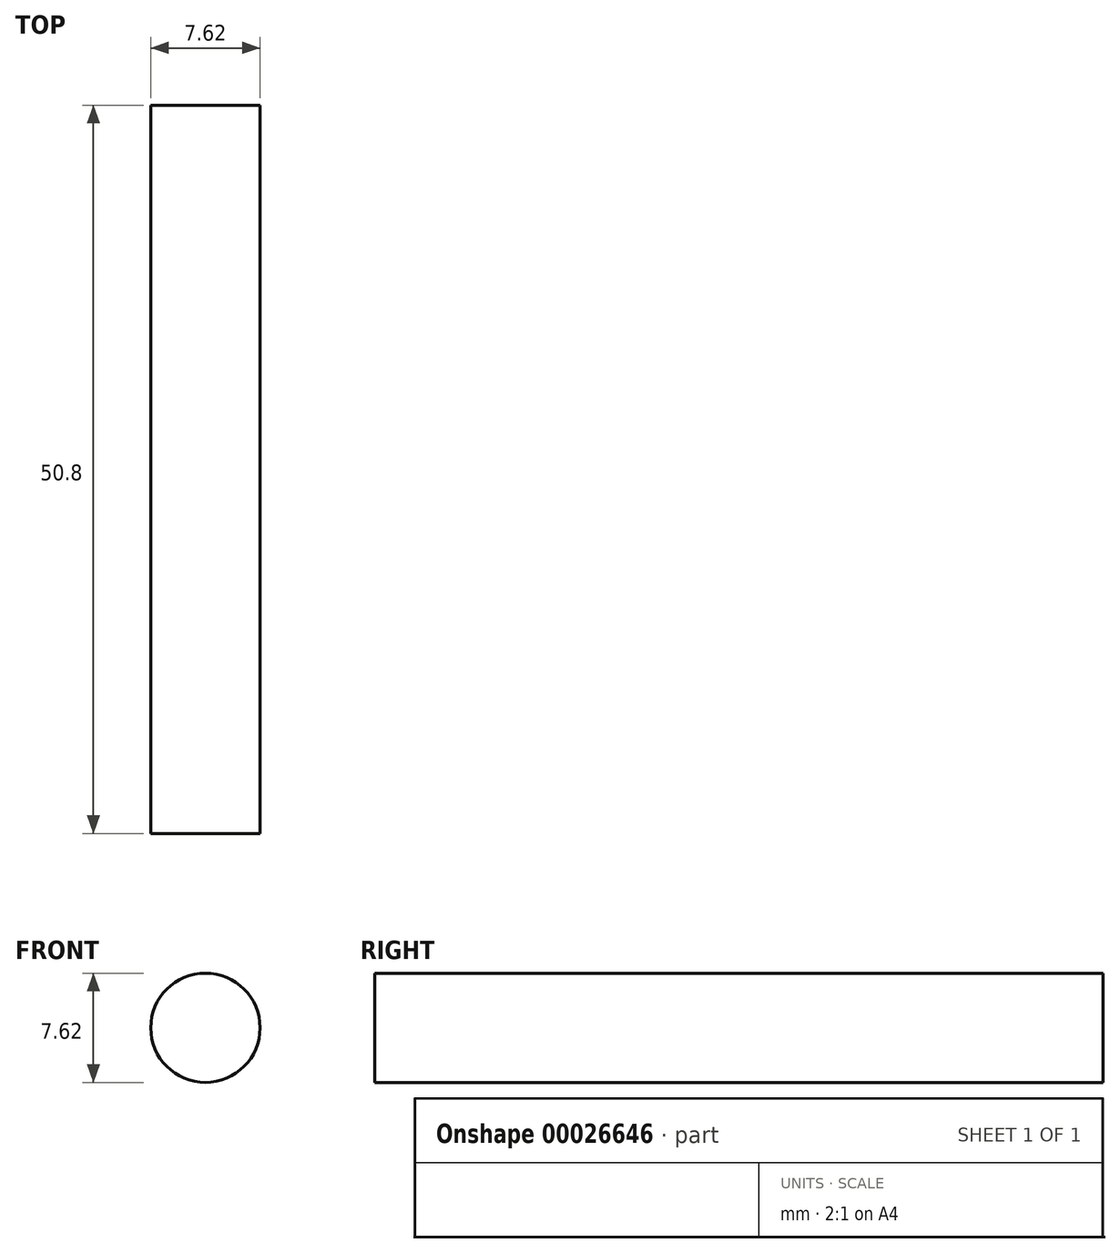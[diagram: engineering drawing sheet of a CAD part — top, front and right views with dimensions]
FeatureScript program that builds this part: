
annotation { "Feature Type Name" : "Feature", "Feature Type Description" : "" }
export const myFeature = defineFeature(function(context is Context, id is Id, definition is map)
    precondition{}
    {
        {
            var Q0;
            Q0=qCreatedBy(makeId("Front.planeOp"),FACE);
            var sketch = newSketch(context, id + "F0", { "sketchPlane" : qUnion([Q0])});
            skCircle(sketch, "E0", {"center": v(0, 30.66) * mm, "radius": 3.81 * mm});
            skSolve(sketch);
        }
        {
            var Q0;
            Q0=makeQuery(id+"F0.imprint","IMPRINT",FACE,{"disambiguationData":[TD([[makeQuery(id+"F0.imprint","IMPRINT",EDGE,{"derivedFrom":sQuery(id+"F0.wireOp",EDGE,"E0")}),1.0]])]});
            extrude(context, id + "F1", {"entities" : qUnion([Q0]), "depth" : 50.8 * mm});
        }
    });
